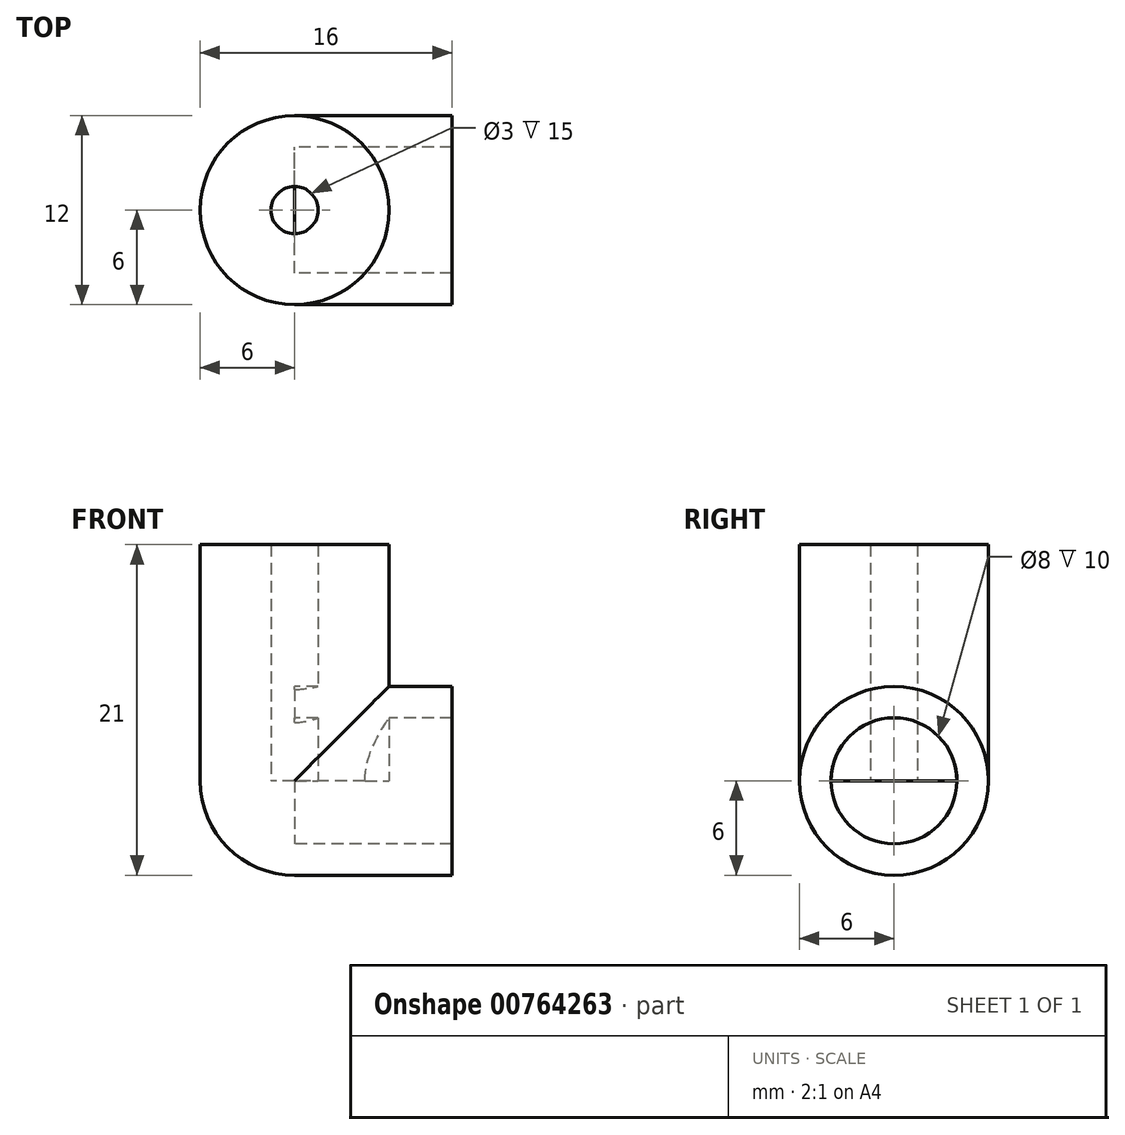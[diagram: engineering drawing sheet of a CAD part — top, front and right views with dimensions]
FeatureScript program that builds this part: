
annotation { "Feature Type Name" : "Feature", "Feature Type Description" : "" }
export const myFeature = defineFeature(function(context is Context, id is Id, definition is map)
    precondition{}
    {
        {
            var Q0;
            Q0=qCreatedBy(makeId("Top.planeOp"),FACE);
            var sketch = newSketch(context, id + "F0", { "sketchPlane" : qUnion([Q0])});
            skCircle(sketch, "E0", {"center": v(0, 0) * mm, "radius": 1.5 * mm});
            skCircle(sketch, "E1", {"center": v(0, 0) * mm, "radius": 6 * mm});
            skSolve(sketch);
        }
        {
            var Q0;
            Q0 = qSketchRegion(id + "F0", true);
            extrude(context, id + "F1", {"entities" : qUnion([Q0]), "depth" : 15 * mm, "offsetDistance" : 25 * mm});
        }
        {
            var Q0;
            Q0=qCreatedBy(makeId("Right.planeOp"),FACE);
            var sketch = newSketch(context, id + "F2", { "sketchPlane" : qUnion([Q0])});
            skCircle(sketch, "E2", {"center": v(0, 0) * mm, "radius": 6 * mm});
            skCircle(sketch, "E3", {"center": v(0, 0) * mm, "radius": 4 * mm});
            skSolve(sketch);
        }
        {
            var Q0;
            Q0 = qSketchRegion(id + "F2", true);
            extrude(context, id + "F3", {"entities" : qUnion([Q0]), "operationType" : NewBodyOperationType.ADD, "depth" : 10 * mm, "offsetDistance" : 25 * mm});
        }
        {
            var Q0;
            Q0=makeQuery(id+"F1.opExtrude","CAP_FACE",FACE,{"disambiguationData":[OSD([sQuery(id+"F0.wireOp",EDGE,"E0"),sQuery(id+"F0.wireOp",EDGE,"E1")])],"isStart":true});
            var sketch = newSketch(context, id + "F4", { "sketchPlane" : qUnion([Q0])});
            skArc(sketch, "E4", {"start": v(0, 6) * mm, "mid": v(-6, 0) * mm, "end": v(0, -6) * mm});
            skLineSegment(sketch, "E5", {"start": v(0, 6) * mm, "end": v(0, -6) * mm});
            skSolve(sketch);
        }
        {
            var Q0;
            {var subQ9=sQuery(id+"F4.wireOp",EDGE,"E4");Q0=makeQuery(id+"F4.imprint","IMPRINT",FACE,{"disambiguationData":[TD([[makeQuery(id+"F4.imprint","IMPRINT",EDGE,{"derivedFrom":subQ9}),-1.0]])]});}
            var sketch = newSketch(context, id + "F5", { "sketchPlane" : qUnion([Q0])});
            skLineSegment(sketch, "E6", {"start": v(0, -10.2) * mm, "end": v(0, 14.03) * mm});
            skSolve(sketch);
        }
        {
            var Q0;
            Q0 = qSketchRegion(id + "F4", true);
            var Q1;
            Q1=sQuery(id+"F5.wireOp",EDGE,"E6");
            revolve(context, id + "F6", {"operationType" : NewBodyOperationType.ADD, "surfaceOperationType" : NewSurfaceOperationType.NEW, "entities" : qUnion([Q0]), "axis" : qUnion([Q1]), "revolveType" : RevolveType.ONE_DIRECTION, "angle" : 90 * degree});
        }
    });
